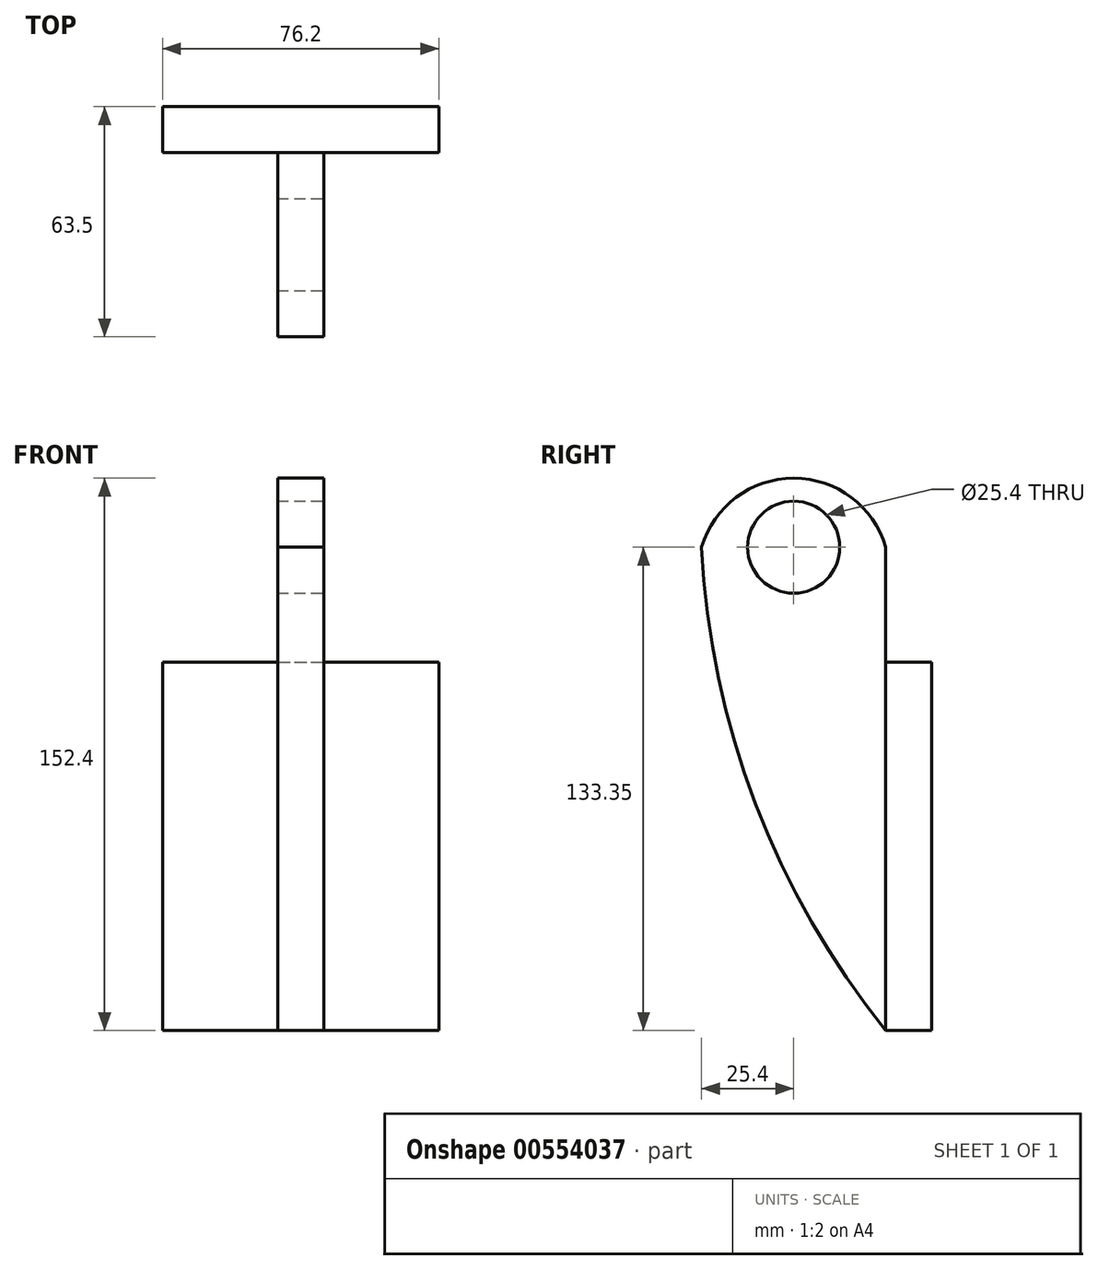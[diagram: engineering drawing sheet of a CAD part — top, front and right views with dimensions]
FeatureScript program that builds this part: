
annotation { "Feature Type Name" : "Feature", "Feature Type Description" : "" }
export const myFeature = defineFeature(function(context is Context, id is Id, definition is map)
    precondition{}
    {
        {
            var Q0;
            Q0=qCreatedBy(makeId("Front.planeOp"),FACE);
            var sketch = newSketch(context, id + "F0", { "sketchPlane" : qUnion([Q0])});
            skLineSegment(sketch, "E0.bottom", {"start": v(-38.1, 50.8) * mm, "end": v(38.1, 50.8) * mm});
            skLineSegment(sketch, "E0.top", {"start": v(-38.1, -50.8) * mm, "end": v(38.1, -50.8) * mm});
            skLineSegment(sketch, "E0.left", {"start": v(-38.1, 50.8) * mm, "end": v(-38.1, -50.8) * mm});
            skLineSegment(sketch, "E0.right", {"start": v(38.1, 50.8) * mm, "end": v(38.1, -50.8) * mm});
            skPoint(sketch, "E0.middle", {"position": v(0, 0) * mm});
            skSolve(sketch);
        }
        {
            var Q0;
            Q0 = qSketchRegion(id + "F0", true);
            extrude(context, id + "F1", {"entities" : qUnion([Q0]), "depth" : 12.7 * mm, "offsetDistance" : 25.4 * mm});
        }
        {
            var Q0;
            Q0=makeQuery(id+"F1.opExtrude","CAP_FACE",FACE,{"disambiguationData":[OSD([sQuery(id+"F0.wireOp",EDGE,"E0.bottom"),sQuery(id+"F0.wireOp",EDGE,"E0.top"),sQuery(id+"F0.wireOp",EDGE,"E0.left"),sQuery(id+"F0.wireOp",EDGE,"E0.right")])],"isStart":false});
            var sketch = newSketch(context, id + "F2", { "sketchPlane" : qUnion([Q0])});
            skLineSegment(sketch, "E1.bottom", {"start": v(6.35, 50.8) * mm, "end": v(-6.35, 50.8) * mm});
            skLineSegment(sketch, "E1.top", {"start": v(6.35, -50.8) * mm, "end": v(-6.35, -50.8) * mm});
            skLineSegment(sketch, "E1.left", {"start": v(6.35, 50.8) * mm, "end": v(6.35, -50.8) * mm});
            skLineSegment(sketch, "E1.right", {"start": v(-6.35, 50.8) * mm, "end": v(-6.35, -50.8) * mm});
            skPoint(sketch, "E1.middle", {"position": v(0, 0) * mm});
            skSolve(sketch);
        }
        {
            var Q0;
            Q0=makeQuery(id+"F2.imprint","IMPRINT",FACE,{"disambiguationData":[TD([[makeQuery(id+"F2.imprint","IMPRINT",EDGE,{"derivedFrom":sQuery(id+"F2.wireOp",EDGE,"E1.bottom")}),-1.0]])]});
            extrude(context, id + "F3", {"entities" : qUnion([Q0]), "operationType" : NewBodyOperationType.ADD, "depth" : 50.8 * mm, "offsetDistance" : 25.4 * mm});
        }
        {
            var Q0;
            Q0=makeQuery(id+"F3.boolean.opBoolean","MERGE",FACE,{"derivedFrom":[makeQuery(id+"F1.opExtrude","SWEPT_FACE",FACE,{"disambiguationData":[OSD([sQuery(id+"F0.wireOp",EDGE,"E0.bottom")])]}),makeQuery(id+"F3.opExtrude","SWEPT_FACE",FACE,{"disambiguationData":[OSD([sQuery(id+"F2.wireOp",EDGE,"E1.bottom")])]})]});
            var sketch = newSketch(context, id + "F4", { "sketchPlane" : qUnion([Q0])});
            skLineSegment(sketch, "E2", {"start": v(-6.35, -12.7) * mm, "end": v(6.35, -12.7) * mm});
            skLineSegment(sketch, "E3", {"start": v(6.35, -12.7) * mm, "end": v(6.35, -63.5) * mm});
            skLineSegment(sketch, "E4", {"start": v(6.35, -63.5) * mm, "end": v(-6.35, -63.5) * mm});
            skLineSegment(sketch, "E5", {"start": v(-6.35, -63.5) * mm, "end": v(-6.35, -12.7) * mm});
            skSolve(sketch);
        }
        {
            var Q0;
            Q0 = qSketchRegion(id + "F4", true);
            extrude(context, id + "F5", {"entities" : qUnion([Q0]), "operationType" : NewBodyOperationType.ADD, "depth" : 50.8 * mm, "offsetDistance" : 25.4 * mm});
        }
        {
            var Q0;
            Q0=makeQuery(id+"F5.boolean.opBoolean","MERGE",FACE,{"derivedFrom":[makeQuery(id+"F3.opExtrude","SWEPT_FACE",FACE,{"disambiguationData":[OSD([sQuery(id+"F2.wireOp",EDGE,"E1.left")])]}),makeQuery(id+"F5.opExtrude","SWEPT_FACE",FACE,{"disambiguationData":[OSD([sQuery(id+"F4.wireOp",EDGE,"E3")])]})]});
            var sketch = newSketch(context, id + "F6", { "sketchPlane" : qUnion([Q0])});
            skLineSegment(sketch, "E6", {"start": v(-38.1, 101.6) * mm, "end": v(-38.1, 69.85) * mm, "construction": true});
            skLineSegment(sketch, "E7", {"start": v(-38.1, 101.6) * mm, "end": v(-38.1, 95.25) * mm, "construction": true});
            skLineSegment(sketch, "E8", {"start": v(-38.1, 95.25) * mm, "end": v(-38.1, 69.85) * mm, "construction": true});
            skCircle(sketch, "E9", {"center": v(-38.1, 82.55) * mm, "radius": 12.7 * mm});
            skArc(sketch, "E10", {"start": v(-12.7, 82.55) * mm, "mid": v(-38.1, 101.6) * mm, "end": v(-63.5, 82.55) * mm});
            skLineSegment(sketch, "E11", {"start": v(-63.5, 82.55) * mm, "end": v(-76.8, 103.25) * mm});
            skLineSegment(sketch, "E12", {"start": v(-76.8, 103.25) * mm, "end": v(0, 103.25) * mm});
            skLineSegment(sketch, "E13", {"start": v(0, 103.25) * mm, "end": v(-12.7, 82.55) * mm});
            skArc(sketch, "E14", {"start": v(-63.5, 82.55) * mm, "mid": v(-48.64, 11.86) * mm, "end": v(-12.7, -50.8) * mm});
            skLineSegment(sketch, "E15", {"start": v(-63.5, 82.55) * mm, "end": v(-133.59, -36.49) * mm});
            skLineSegment(sketch, "E16", {"start": v(-133.59, -36.49) * mm, "end": v(-38.8, -66.67) * mm});
            skLineSegment(sketch, "E17", {"start": v(-38.8, -66.67) * mm, "end": v(-12.7, -50.8) * mm});
            skSolve(sketch);
        }
        {
            var Q0;
            Q0 = qSketchRegion(id + "F6", true);
            extrude(context, id + "F7", {"entities" : qUnion([Q0]), "operationType" : NewBodyOperationType.REMOVE, "oppositeDirection" : true, "depth" : 25.4 * mm, "offsetDistance" : 25.4 * mm});
        }
    });
